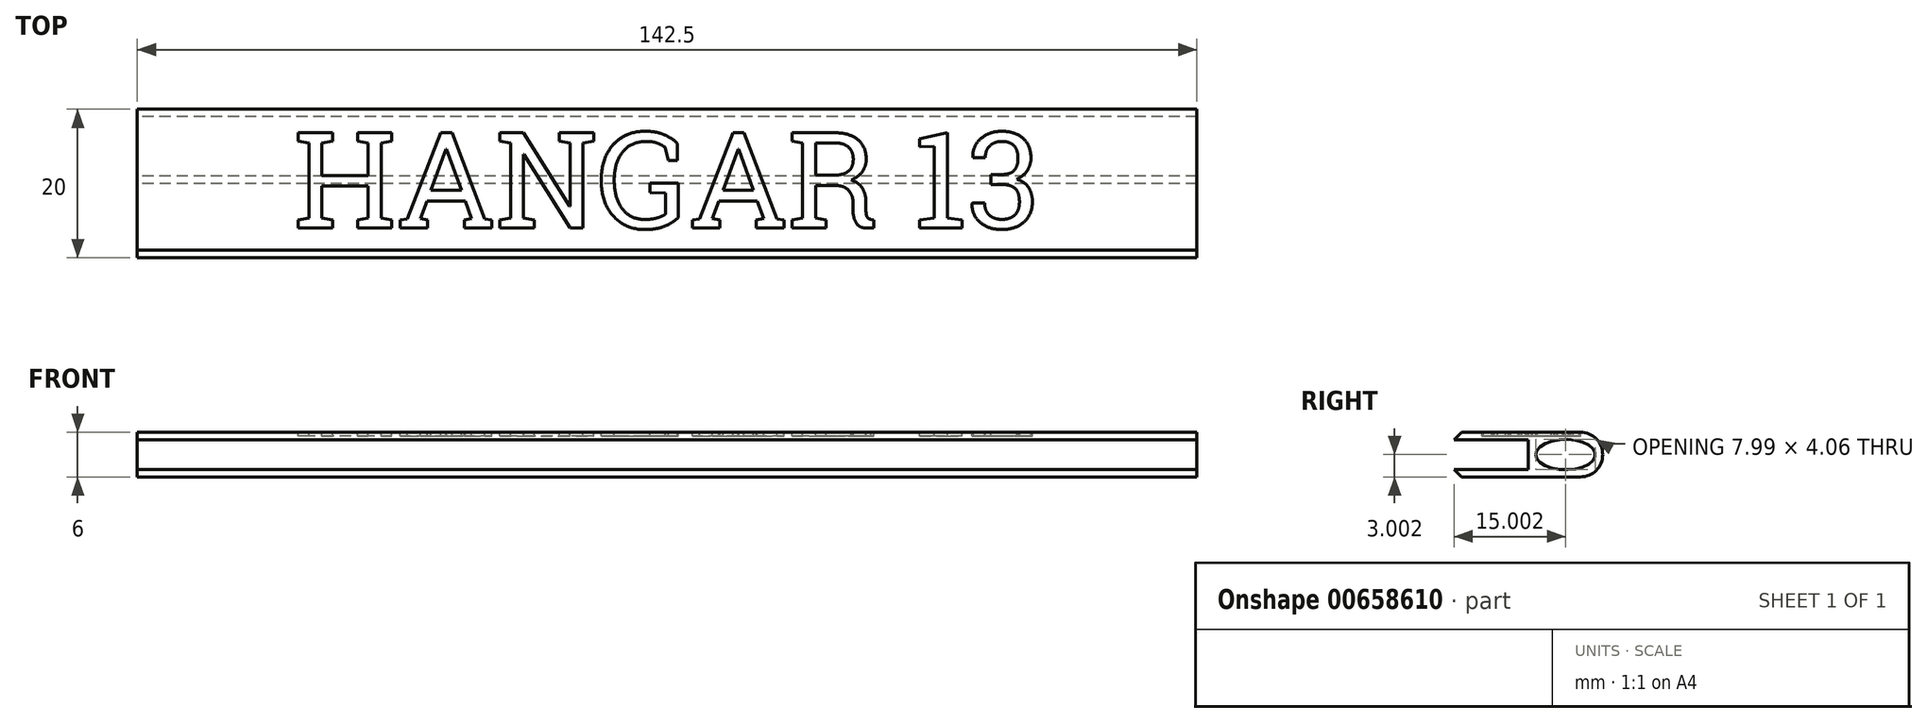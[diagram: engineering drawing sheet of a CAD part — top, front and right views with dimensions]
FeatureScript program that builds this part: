
annotation { "Feature Type Name" : "Feature", "Feature Type Description" : "" }
export const myFeature = defineFeature(function(context is Context, id is Id, definition is map)
    precondition{}
    {
        {
            var Q0;
            Q0=qCreatedBy(makeId("Right.planeOp"),FACE);
            var sketch = newSketch(context, id + "F0", { "sketchPlane" : qUnion([Q0])});
            skLineSegment(sketch, "E0", {"start": v(3.04, 2.4) * mm, "end": v(23.04, 2.4) * mm});
            skLineSegment(sketch, "E1", {"start": v(23.04, 2.4) * mm, "end": v(23.04, 8.4) * mm});
            skLineSegment(sketch, "E2", {"start": v(23.04, 8.4) * mm, "end": v(3.04, 8.4) * mm});
            skLineSegment(sketch, "E3", {"start": v(3.04, 8.4) * mm, "end": v(3.04, 7.4) * mm});
            skLineSegment(sketch, "E4", {"start": v(3.04, 7.4) * mm, "end": v(13.04, 7.4) * mm});
            skLineSegment(sketch, "E5", {"start": v(13.04, 7.4) * mm, "end": v(13.04, 3.4) * mm});
            skLineSegment(sketch, "E6", {"start": v(13.04, 3.4) * mm, "end": v(3.04, 3.4) * mm});
            skLineSegment(sketch, "E7", {"start": v(3.04, 3.4) * mm, "end": v(3.04, 2.4) * mm});
            skLineSegment(sketch, "E8.bottom", {"start": v(13.04, 7.4) * mm, "end": v(22.04, 7.4) * mm, "construction": true});
            skLineSegment(sketch, "E8.top", {"start": v(13.04, 3.4) * mm, "end": v(22.04, 3.4) * mm, "construction": true});
            skLineSegment(sketch, "E8.right", {"start": v(22.04, 7.4) * mm, "end": v(22.04, 3.4) * mm, "construction": true});
            skLineSegment(sketch, "E9.bottom", {"start": v(13.04, 7.4) * mm, "end": v(14.04, 7.4) * mm});
            skLineSegment(sketch, "E9.top", {"start": v(13.04, 3.4) * mm, "end": v(14.04, 3.4) * mm});
            skLineSegment(sketch, "E9.right", {"start": v(14.04, 7.4) * mm, "end": v(14.04, 3.4) * mm, "construction": true});
            skLineSegment(sketch, "E10", {"start": v(14.04, 7.4) * mm, "end": v(22.04, 3.4) * mm, "construction": true});
            skEllipse(sketch, "E11", {"center": v(18.04, 5.4) * mm, "majorRadius": 4 * mm, "minorRadius": 2.03 * mm, "majorAxis": v(-1, 0)});
            skSolve(sketch);
        }
        {
            var Q0;
            Q0 = qSketchRegion(id + "F0", true);
            extrude(context, id + "F1", {"entities" : qUnion([Q0]), "depth" : 142.5 * mm, "offsetDistance" : 25 * mm});
        }
        {
            var Q0;
            Q0=makeQuery(id+"F1.opExtrude","SWEPT_EDGE",EDGE,{"disambiguationData":[OSD([sQuery(id+"F0.wireOp",EDGE,"E2"),sQuery(id+"F0.wireOp",EDGE,"E3")])]});
            var Q1;
            Q1=makeQuery(id+"F1.opExtrude","SWEPT_EDGE",EDGE,{"disambiguationData":[OSD([sQuery(id+"F0.wireOp",EDGE,"E0"),sQuery(id+"F0.wireOp",EDGE,"E7")])]});
            chamfer(context, id + "F2", {"entities" : qUnion([Q0, Q1]), "width" : 1 * mm, "tangentPropagation" : true});
        }
        {
            var Q0;
            Q0=makeQuery(id+"F1.opExtrude","SWEPT_EDGE",EDGE,{"disambiguationData":[OSD([sQuery(id+"F0.wireOp",EDGE,"E1"),sQuery(id+"F0.wireOp",EDGE,"E2")])]});
            var Q1;
            Q1=makeQuery(id+"F1.opExtrude","SWEPT_EDGE",EDGE,{"disambiguationData":[OSD([sQuery(id+"F0.wireOp",EDGE,"E0"),sQuery(id+"F0.wireOp",EDGE,"E1")])]});
            fillet(context, id + "F3", {"entities" : qUnion([Q0, Q1]), "radius" : 3 * mm, "tangentPropagation" : true, "allowEdgeOverflow" : false});
        }
        {
            var Q0;
            Q0=makeQuery(id+"F0.imprint","IMPRINT",FACE,{"disambiguationData":[TD([[makeQuery(id+"F0.imprint","IMPRINT",EDGE,{"derivedFrom":sQuery(id+"F0.wireOp",EDGE,"E11")}),1.0]])]});
            extrude(context, id + "F4", {"entities" : qUnion([Q0]), "operationType" : NewBodyOperationType.REMOVE, "depth" : 142.5 * mm, "offsetDistance" : 25 * mm});
        }
        {
            var Q0;
            Q0=makeQuery(id+"F1.opExtrude","SWEPT_FACE",FACE,{"disambiguationData":[OSD([sQuery(id+"F0.wireOp",EDGE,"E2")])]});
            var sketch = newSketch(context, id + "F5", { "sketchPlane" : qUnion([Q0])});
            skText(sketch, "E12", { "text": "HANGAR 13", "fontName": "RobotoSlab-Regular.ttf"});
            skLineSegment(sketch, "E13", {"start": v(142.5, 12.04) * mm, "end": v(121.5, 12.04) * mm});
            skLineSegment(sketch, "E14", {"start": v(0, 12.04) * mm, "end": v(21, 12.04) * mm});
            const initialGuessF5  = {"E12": [0.021, 0.00702, 1, 0, 0.01302]};
            skSetInitialGuess(sketch, initialGuessF5);
            skSolve(sketch);
        }
        {
            var Q0;
            Q0 = qSketchRegion(id + "F5", true);
            extrude(context, id + "F6", {"entities" : qUnion([Q0]), "operationType" : NewBodyOperationType.REMOVE, "oppositeDirection" : true, "depth" : 0.5 * mm, "offsetDistance" : 25 * mm});
        }
    });
